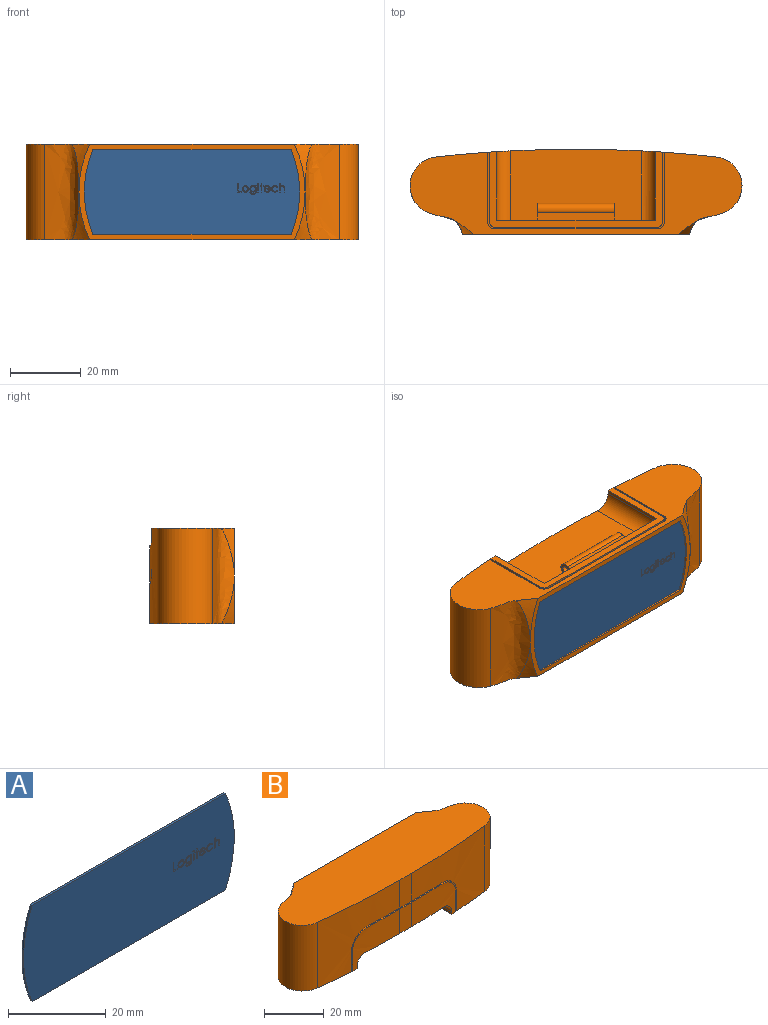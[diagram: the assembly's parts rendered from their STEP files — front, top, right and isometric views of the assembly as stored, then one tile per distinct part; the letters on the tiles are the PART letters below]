
ASSEMBLY  parts=2 mates=1
PART A: 110 faces, bbox 61x0.5x24.2 mm
  f0: plane 61x24.19mm, normal (0,-1,0), area 1424.4mm2, adj f1,f2,f3,f4,f6,f7,f8,f9
  f1: cylinder r=30.5mm len=24.19mm, axis (0,1,0), area 12.4mm2, adj f0,f2,f4,f5
  f2: plane 56x0.5mm, normal (0,0,-1), area 28mm2, adj f0,f1,f3,f5
  f3: cylinder r=30.5mm len=24.19mm, axis (0,1,0), area 12.4mm2, adj f0,f2,f4,f5
  f4: plane 56x0.5mm, normal (0,0,1), area 28mm2, adj f0,f1,f3,f5
  f5: plane 61x24.19mm, normal (0,1,0), area 1435.8mm2, adj f1,f2,f3,f4
  f6: plane 2.38x0.01mm, normal (-1,0,0), area 0mm2, adj f0,f7,f11,f12
  f7: plane 1.13x0.01mm, normal (0,0,-1), area 0mm2, adj f0,f6,f8,f12
  f8: plane 0.24x0.01mm, normal (1,0,0), area 0mm2, adj f0,f7,f9,f12
  f9: plane 0.92x0.01mm, normal (0,0,1), area 0mm2, adj f0,f8,f10,f12
  f10: plane 2.14x0.01mm, normal (1,0,0), area 0mm2, adj f0,f9,f11,f12
  f11: plane 0.21x0.01mm, normal (0,0,1), area 0mm2, adj f0,f6,f10,f12
  f12: plane 2.38x1.13mm, normal (0,-1,0), area 0.7mm2, adj f6,f7,f8,f9,f10,f11
  f13: plane 1.8x1.8mm, normal (0,-1,0), area 1.1mm2, adj f14,f15,f16,f17,f18,f19,f20,f21
  f14: cylinder r=0.86mm len=0.66mm, axis (0,1,0), area 0mm2, adj f0,f13,f15,f19
  f15: cylinder r=0.89mm len=0.62mm, axis (0,1,0), area 0mm2, adj f0,f13,f14,f16
  f16: extruded ~0.9x0.9mm, area 0mm2, adj f0,f13,f15,f17
  f17: extruded ~0.9x0.9mm, area 0mm2, adj f0,f13,f16,f18
  f18: cylinder r=0.89mm len=0.62mm, axis (0,1,0), area 0mm2, adj f0,f13,f17,f19
  f19: cylinder r=0.86mm len=0.66mm, axis (0,1,0), area 0mm2, adj f0,f13,f14,f18
  f20: extruded ~0.69x0.69mm, area 0mm2, adj f13,f21,f23,f24
  f21: extruded ~0.69x0.69mm, area 0mm2, adj f13,f20,f22,f24
  f22: cylinder r=0.67mm len=0.69mm, axis (0,-1,0), area 0mm2, adj f13,f21,f23,f24
  f23: cylinder r=0.67mm len=0.69mm, axis (0,-1,0), area 0mm2, adj f13,f20,f22,f24
  f24: plane 1.37x1.37mm, normal (0,-1,0), area 1.5mm2, adj f20,f21,f22,f23
  f25: plane 2.44x1.8mm, normal (0,-1,0), area 1.7mm2, adj f26,f27,f28,f29,f30,f31,f32,f33
  f26: plane 0.3x0.01mm, normal (-1,0,0), area 0mm2, adj f0,f25,f27,f39
  f27: extruded ~0.69x0.34mm, area 0mm2, adj f0,f25,f26,f28
  f28: extruded ~0.9x0.9mm, area 0mm2, adj f0,f25,f27,f29
  f29: extruded ~0.89x0.88mm, area 0mm2, adj f0,f25,f28,f30
  f30: cylinder r=0.87mm len=0.7mm, axis (0,1,0), area 0mm2, adj f0,f25,f29,f31
  f31: plane 0.09x0.01mm, normal (-1,0,0), area 0mm2, adj f0,f25,f30,f32
  f32: extruded ~0.7x0.69mm, area 0mm2, adj f0,f25,f31,f33
  f33: extruded ~0.65x0.34mm, area 0mm2, adj f0,f25,f32,f34
  f34: plane 0.21x0.01mm, normal (0,0,1), area 0mm2, adj f0,f25,f33,f35
  f35: extruded ~0.89x0.55mm, area 0mm2, adj f0,f25,f34,f36
  f36: extruded ~0.82x0.5mm, area 0mm2, adj f0,f25,f35,f37
  f37: extruded ~0.53x0.06mm, area 0mm2, adj f0,f25,f36,f38
  f38: plane 1.38x0.01mm, normal (1,0,0), area 0mm2, adj f0,f25,f37,f39
  f39: plane 0.21x0.01mm, normal (0,0,1), area 0mm2, adj f0,f25,f26,f38
  f40: extruded ~0.68x0.67mm, area 0mm2, adj f25,f41,f43,f44
  f41: extruded ~0.7x0.69mm, area 0mm2, adj f25,f40,f42,f44
  f42: extruded ~0.69x0.65mm, area 0mm2, adj f25,f41,f43,f44
  f43: extruded ~0.68x0.67mm, area 0mm2, adj f25,f40,f42,f44
  f44: plane 1.37x1.34mm, normal (0,-1,0), area 1.5mm2, adj f40,f41,f42,f43
  f45: extruded ~0.2x0.18mm, area 0mm2, adj f0,f46,f48,f49
  f46: extruded ~0.2x0.18mm, area 0mm2, adj f0,f45,f47,f49
  f47: extruded ~0.2x0.18mm, area 0mm2, adj f0,f46,f48,f49
  f48: extruded ~0.2x0.18mm, area 0mm2, adj f0,f45,f47,f49
  f49: plane 0.4x0.37mm, normal (0,-1,0), area 0.1mm2, adj f45,f46,f47,f48
  f50: plane 1.74x0.01mm, normal (-1,0,0), area 0mm2, adj f0,f51,f53,f54
  f51: plane 0.21x0.01mm, normal (0,0,-1), area 0mm2, adj f0,f50,f52,f54
  f52: plane 1.74x0.01mm, normal (1,0,0), area 0mm2, adj f0,f51,f53,f54
  f53: plane 0.21x0.01mm, normal (0,0,1), area 0mm2, adj f0,f50,f52,f54
  f54: plane 1.74x0.21mm, normal (0,-1,0), area 0.4mm2, adj f50,f51,f52,f53
  f55: plane 0.7x0.01mm, normal (-1,0,0), area 0mm2, adj f0,f56,f66,f67
  f56: plane 0.31x0.01mm, normal (0,0,1), area 0mm2, adj f0,f55,f57,f67
  f57: plane 0.21x0.01mm, normal (-1,0,0), area 0mm2, adj f0,f56,f58,f67
  f58: plane 0.31x0.01mm, normal (0,0,-1), area 0mm2, adj f0,f57,f59,f67
  f59: plane 1.53x0.01mm, normal (-1,0,0), area 0mm2, adj f0,f58,f60,f67
  f60: plane 0.21x0.01mm, normal (0,0,-1), area 0mm2, adj f0,f59,f61,f67
  f61: plane 1.53x0.01mm, normal (1,0,0), area 0mm2, adj f0,f60,f62,f67
  f62: plane 0.31x0.01mm, normal (0,0,-1), area 0mm2, adj f0,f61,f63,f67
  f63: plane 0.21x0.01mm, normal (1,0,0), area 0mm2, adj f0,f62,f64,f67
  f64: plane 0.31x0.01mm, normal (0,0,1), area 0mm2, adj f0,f63,f65,f67
  f65: plane 0.7x0.01mm, normal (1,0,0), area 0mm2, adj f0,f64,f66,f67
  f66: plane 0.21x0.01mm, normal (0,0,1), area 0mm2, adj f0,f55,f65,f67
  f67: plane 2.44x0.82mm, normal (0,-1,0), area 0.7mm2, adj f55,f56,f57,f58,f59,f60,f61,f62
  f68: plane 1.8x1.77mm, normal (0,-1,0), area 1.3mm2, adj f69,f70,f71,f72,f73,f74,f75,f76
  f69: extruded ~0.64x0.37mm, area 0mm2, adj f0,f68,f70,f78
  f70: extruded ~0.64x0.64mm, area 0mm2, adj f0,f68,f69,f71
  f71: plane 1.56x0.01mm, normal (0,0,-1), area 0mm2, adj f0,f68,f70,f72
  f72: extruded ~0.6x0.19mm, area 0mm2, adj f0,f68,f71,f73
  f73: extruded ~0.7x0.34mm, area 0mm2, adj f0,f68,f72,f74
  f74: extruded ~0.68x0.32mm, area 0mm2, adj f0,f68,f73,f75
  f75: cylinder r=0.92mm len=0.58mm, axis (0,1,0), area 0mm2, adj f0,f68,f74,f76
  f76: extruded ~0.9x0.88mm, area 0mm2, adj f0,f68,f75,f77
  f77: extruded ~0.8x0.48mm, area 0mm2, adj f0,f68,f76,f78
  f78: plane 0.19x0.1mm, normal (0.46,0,0.89), area 0mm2, adj f0,f68,f69,f77
  f79: plane 1.32x0.01mm, normal (0,0,1), area 0mm2, adj f68,f80,f82,f83
  f80: extruded ~0.67x0.52mm, area 0mm2, adj f68,f79,f81,f83
  f81: cylinder r=0.66mm len=0.45mm, axis (0,-1,0), area 0mm2, adj f68,f80,f82,f83
  f82: extruded ~0.36x0.21mm, area 0mm2, adj f68,f79,f81,f83
  f83: plane 1.32x0.52mm, normal (0,-1,0), area 0.5mm2, adj f79,f80,f81,f82
  f84: extruded ~0.8x0.41mm, area 0mm2, adj f0,f85,f93,f94
  f85: extruded ~0.97x0.92mm, area 0mm2, adj f0,f84,f86,f94
  f86: extruded ~0.96x0.89mm, area 0mm2, adj f0,f85,f87,f94
  f87: extruded ~0.81x0.4mm, area 0mm2, adj f0,f86,f88,f94
  f88: plane 0.18x0.12mm, normal (0.55,0,0.84), area 0mm2, adj f0,f87,f89,f94
  f89: cylinder r=0.78mm len=0.63mm, axis (0,-1,0), area 0mm2, adj f0,f88,f90,f94
  f90: extruded ~0.75x0.69mm, area 0mm2, adj f0,f89,f91,f94
  f91: extruded ~0.74x0.68mm, area 0mm2, adj f0,f90,f92,f94
  f92: extruded ~0.63x0.31mm, area 0mm2, adj f0,f91,f93,f94
  f93: plane 0.18x0.11mm, normal (0.53,0,-0.85), area 0mm2, adj f0,f84,f92,f94
  f94: plane 1.8x1.77mm, normal (0,-1,0), area 0.9mm2, adj f84,f85,f86,f87,f88,f89,f90,f91
  f95: plane 2.44x0.01mm, normal (-1,0,0), area 0mm2, adj f0,f96,f108,f109
  f96: plane 0.21x0.01mm, normal (0,0,-1), area 0mm2, adj f0,f95,f97,f109
  f97: plane 0.63x0.01mm, normal (1,0,0), area 0mm2, adj f0,f96,f98,f109
  f98: extruded ~0.47x0.03mm, area 0mm2, adj f0,f97,f99,f109
  f99: extruded ~0.59x0.46mm, area 0mm2, adj f0,f98,f100,f109
  f100: extruded ~0.45x0.34mm, area 0mm2, adj f0,f99,f101,f109
  f101: extruded ~0.4x0.03mm, area 0mm2, adj f0,f100,f102,f109
  f102: plane 0.82x0.01mm, normal (-1,0,0), area 0mm2, adj f0,f101,f103,f109
  f103: plane 0.21x0.01mm, normal (0,0,-1), area 0mm2, adj f0,f102,f104,f109
  f104: plane 0.89x0.01mm, normal (1,0,0), area 0mm2, adj f0,f103,f105,f109
  f105: extruded ~0.88x0.65mm, area 0mm2, adj f0,f104,f106,f109
  f106: extruded ~0.66x0.36mm, area 0mm2, adj f0,f105,f107,f109
  f107: plane 1.03x0.01mm, normal (1,0,0), area 0mm2, adj f0,f106,f108,f109
  f108: plane 0.21x0.01mm, normal (0,0,1), area 0mm2, adj f0,f95,f107,f109
  f109: plane 2.44x1.53mm, normal (0,-1,0), area 1.1mm2, adj f95,f96,f97,f98,f99,f100,f101,f102
PART B: 77 faces, bbox 94x24x34.7 mm
  f0: plane 45x5mm, normal (0,-1,0), area 152.1mm2, adj f1,f59,f60,f61,f62,f63,f71,f72
  f1: plane 49x21.4mm, normal (0,0,-1), area 174.4mm2, adj f0,f14,f17,f54,f58,f59,f63,f64
  f2: plane 50x15mm, normal (0,-1,0), area 36.4mm2, adj f49,f50,f51,f52,f53,f54,f55,f56
  f3: plane 11.5x5.57mm, normal (0,-1,0), area 64.1mm2, adj f4,f5,f10,f51
  f4: cylinder r=322mm len=36.95mm, axis (0,0,1), area 667.3mm2, adj f3,f9,f10,f15,f49,f50,f51
  f5: cylinder r=322mm len=36.95mm, axis (0,0,1), area 667.3mm2, adj f3,f9,f10,f18,f51,f52,f53
  f6: plane 7x5mm, normal (0,1,0), area 12.6mm2, adj f42,f43,f45,f47
  f7: plane 31x24mm, normal (0,1,0), area 377.4mm2, adj f24,f26,f28,f31,f33
  f8: plane 24x19.92mm, normal (0,1,0), area 368.6mm2, adj f23,f24,f26,f30
  f9: plane 94.01x23.26mm, normal (0,0,-1), area 849.2mm2, adj f4,f5,f12,f13,f15,f16,f18,f19
  f10: plane 93.99x24mm, normal (0,0,1), area 1961.2mm2, adj f3,f4,f5,f12,f13,f15,f16,f18
  f11: plane 10x5.57mm, normal (0,-1,0), area 55.7mm2, adj f14,f17,f56,f61
  f12: plane 64x27mm, normal (0,1,0), area 250mm2, adj f9,f10,f19,f20,f21,f22,f23,f24
  f13: extruded ~27x9.77mm, area 299.3mm2, adj f9,f10,f15,f21,f22
  f14: cylinder r=322mm len=21.72mm, axis (0,0,1), area 220.2mm2, adj f1,f11,f56,f57,f58,f59,f60,f61
  f15: cylinder r=8.2mm len=27mm, axis (0,0,1), area 587.8mm2, adj f4,f9,f10,f13
  f16: extruded ~27x9.77mm, area 299.3mm2, adj f9,f10,f18,f19,f20
  f17: cylinder r=322mm len=21.72mm, axis (0,0,1), area 220.2mm2, adj f1,f11,f54,f55,f56,f61,f62,f63
  f18: cylinder r=8.2mm len=27mm, axis (0,0,1), area 587.8mm2, adj f5,f9,f10,f16
  f19: revolved ~15.62x7.61mm, area 26.7mm2, adj f9,f12,f16
  f20: revolved ~17.35x7.55mm, area 26.7mm2, adj f10,f12,f16
  f21: revolved ~17.35x7.55mm, area 26.7mm2, adj f9,f12,f13
  f22: revolved ~15.62x7.61mm, area 26.7mm2, adj f10,f12,f13
  f23: cylinder r=30.5mm len=24mm, axis (0,1,0), area 24.7mm2, adj f8,f12,f24,f26
  f24: plane 56.08x2mm, normal (0,0,-1), area 57.6mm2, adj f7,f8,f12,f23,f25,f27,f30,f31
  f25: cylinder r=30.5mm len=24mm, axis (0,1,0), area 24.7mm2, adj f12,f24,f26,f27
  f26: plane 56.08x2mm, normal (0,0,1), area 57.6mm2, adj f7,f8,f12,f23,f25,f27,f30,f31
  f27: plane 24x19.92mm, normal (0,1,0), area 368.6mm2, adj f24,f25,f26,f34
  f28: cylinder r=9.5mm len=19mm, axis (0,1,0), area 59.7mm2, adj f7,f29
  f29: plane 19x19mm, normal (0,1,0), area 56.5mm2, adj f28,f36
  f30: cylinder r=16mm len=24mm, axis (0,1,0), area 27.1mm2, adj f8,f24,f26,f32
  f31: cylinder r=15.5mm len=24mm, axis (0,1,0), area 27.4mm2, adj f7,f24,f26,f32
  f32: plane 24x6.19mm, normal (0,1,0), area 13.6mm2, adj f24,f26,f30,f31
  f33: cylinder r=15.5mm len=24mm, axis (0,1,0), area 27.4mm2, adj f7,f24,f26,f35
  f34: cylinder r=16mm len=24mm, axis (0,1,0), area 27.1mm2, adj f24,f26,f27,f35
  f35: plane 24x6.19mm, normal (0,1,0), area 13.6mm2, adj f24,f26,f33,f34
  f36: cylinder r=8.5mm len=17mm, axis (0,1,0), area 13.4mm2, adj f29,f37
  f37: plane 17x17mm, normal (0,1,0), area 50.3mm2, adj f36,f38
  f38: cylinder r=7.5mm len=15mm, axis (0,1,0), area 11.8mm2, adj f37,f39
  f39: plane 15x15mm, normal (0,1,0), area 44mm2, adj f38,f40
  f40: cylinder r=6.5mm len=13mm, axis (0,1,0), area 10.2mm2, adj f39,f41
  f41: plane 13x13mm, normal (0,1,0), area 69mm2, adj f40,f42,f43,f44,f45
  f42: cylinder r=5mm len=7mm, axis (0,1,0), area 15.5mm2, adj f6,f41,f43,f45
  f43: plane 7.14x2mm, normal (0,0,-1), area 14.3mm2, adj f6,f41,f42,f44,f46
  f44: cylinder r=5mm len=7mm, axis (0,1,0), area 15.5mm2, adj f41,f43,f45,f46
  f45: plane 7.14x2mm, normal (0,0,1), area 14.3mm2, adj f6,f41,f42,f44,f46
  f46: plane 7x5mm, normal (0,1,0), area 12.6mm2, adj f43,f44,f45,f47
  f47: cone r=3.5mm half-angle=56deg, axis (0,1,0), area 31mm2, adj f6,f46,f48
  f48: plane 4.04x4.04mm, normal (0,1,0), area 12.8mm2, adj f47
  f49: plane 19.73x8mm, normal (1,0,0), area 11.6mm2, adj f2,f4,f9,f50,f69,f70
  f50: cylinder r=7.5mm len=7.5mm, axis (0,-1,0), area 4.7mm2, adj f2,f4,f49,f51
  f51: plane 35x1mm, normal (0,0,-1), area 31.7mm2, adj f2,f3,f4,f5,f50,f52
  f52: cylinder r=7.5mm len=7.5mm, axis (0,-1,0), area 4.7mm2, adj f2,f5,f51,f53
  f53: plane 19.73x8mm, normal (-1,0,0), area 11.6mm2, adj f2,f5,f9,f52,f67,f70
  f54: plane 19.77x8mm, normal (1,0,0), area 11.9mm2, adj f1,f2,f17,f55,f66,f70
  f55: cylinder r=7mm len=7mm, axis (0,-1,0), area 4.6mm2, adj f2,f17,f54,f56
  f56: plane 35x1mm, normal (0,0,1), area 31.7mm2, adj f2,f11,f14,f17,f55,f57
  f57: cylinder r=7mm len=7mm, axis (0,-1,0), area 4.6mm2, adj f2,f14,f56,f58
  f58: plane 19.77x8mm, normal (-1,0,0), area 11.9mm2, adj f1,f2,f14,f57,f64,f70
  f59: plane 19.4x1mm, normal (1,0,0), area 19.4mm2, adj f0,f1,f14,f60
  f60: cylinder r=4mm len=19.62mm, axis (0,-1,0), area 122.6mm2, adj f0,f14,f59,f61
  f61: plane 37x20mm, normal (0,0,-1), area 736mm2, adj f0,f11,f14,f17,f60,f62
  f62: cylinder r=4mm len=19.62mm, axis (0,-1,0), area 122.6mm2, adj f0,f17,f61,f63
  f63: plane 19.4x1mm, normal (-1,0,0), area 19.4mm2, adj f0,f1,f17,f62
  f64: cylinder r=1.5mm len=1.5mm, axis (0,0,-1), area 1.2mm2, adj f1,f58,f65,f70
  f65: plane 46x0.5mm, normal (0,1,0), area 23mm2, adj f1,f64,f66,f70
  f66: cylinder r=1.5mm len=1.5mm, axis (0,0,-1), area 1.2mm2, adj f1,f54,f65,f70
  f67: cylinder r=2mm len=2mm, axis (0,0,-1), area 1.6mm2, adj f9,f53,f68,f70
  f68: plane 46x0.5mm, normal (0,-1,0), area 23mm2, adj f9,f67,f69,f70
  f69: cylinder r=2mm len=2mm, axis (0,0,-1), area 1.6mm2, adj f9,f49,f68,f70
  f70: plane 50x21.5mm, normal (0,0,-1), area 45.2mm2, adj f2,f49,f53,f54,f58,f64,f65,f66
  f71: plane 4.75x3.5mm, normal (-1,0,0), area 11mm2, adj f0,f72,f74,f75,f76
  f72: plane 22x2.1mm, normal (0,0,-1), area 46.2mm2, adj f0,f71,f73,f75
  f73: plane 4.75x3.5mm, normal (1,0,0), area 11mm2, adj f0,f72,f74,f75,f76
  f74: plane 22x2.1mm, normal (0,0,1), area 46.2mm2, adj f0,f71,f73,f75
  f75: cylinder r=1.75mm len=22mm, axis (1,0,0), area 162.6mm2, adj f71,f72,f73,f74
  f76: cylinder r=1mm len=22mm, axis (1,0,0), area 138.2mm2, adj f71,f73
PLACE A t=(79.48,5.99,-15.03)mm
PLACE B rot(axis=(1,0,0),180deg) t=(29.48,4.99,-1.53)mm
MATE fastened A.f1 <-> B.f23  axis (0,1,0) through (79.48,5.99,-15.03)mm
